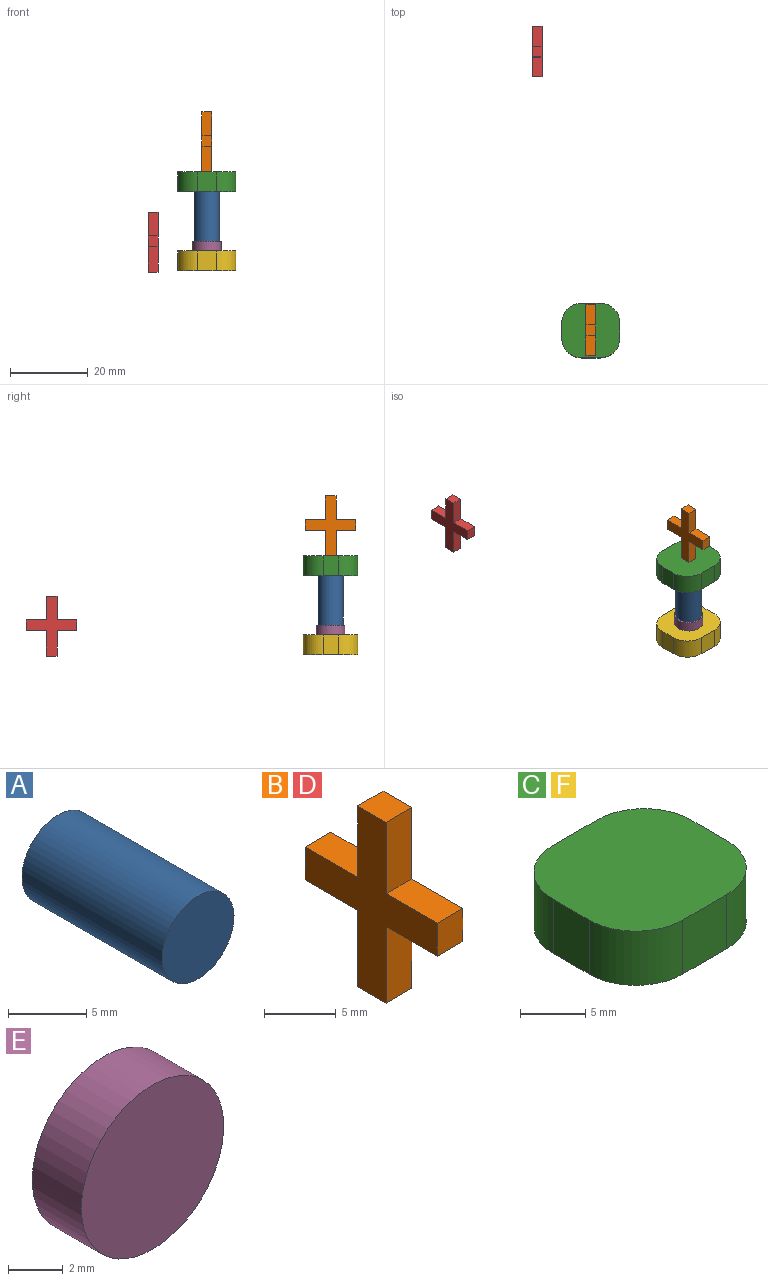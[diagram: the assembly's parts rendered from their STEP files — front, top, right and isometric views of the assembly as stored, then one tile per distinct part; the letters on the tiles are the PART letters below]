
ASSEMBLY  parts=6 mates=4
PART A: 3 faces, bbox 6.5x12.7x6.5 mm
  f0: cylinder r=3.26mm len=12.7mm, axis (0,1,0), area 259.8mm2, adj f1,f2
  f1: plane 6.51x6.51mm, normal (0,-1,0), area 33.3mm2, adj f0
  f2: plane 6.51x6.51mm, normal (0,1,0), area 33.3mm2, adj f0
PART B: 14 faces, bbox 2.5x13x15.4 mm
  f0: plane 2.8x2.54mm, normal (0,0,-1), area 7.1mm2, adj f1,f11,f12,f13
  f1: plane 6.5x2.54mm, normal (0,1,0), area 16.5mm2, adj f0,f2,f12,f13
  f2: plane 5.17x2.54mm, normal (0,0,-1), area 13.1mm2, adj f1,f3,f12,f13
  f3: plane 2.81x2.54mm, normal (0,1,0), area 7.1mm2, adj f2,f4,f12,f13
  f4: plane 5.17x2.54mm, normal (0,0,1), area 13.1mm2, adj f3,f5,f12,f13
  f5: plane 6.09x2.54mm, normal (0,1,0), area 15.5mm2, adj f4,f6,f12,f13
  f6: plane 2.8x2.54mm, normal (0,0,1), area 7.1mm2, adj f5,f7,f12,f13
  f7: plane 6.09x2.54mm, normal (0,-1,0), area 15.5mm2, adj f6,f8,f12,f13
  f8: plane 5.04x2.54mm, normal (0,0,1), area 12.8mm2, adj f7,f9,f12,f13
  f9: plane 2.81x2.54mm, normal (0,-1,0), area 7.1mm2, adj f8,f10,f12,f13
  f10: plane 5.04x2.54mm, normal (0,0,-1), area 12.8mm2, adj f9,f11,f12,f13
  f11: plane 6.5x2.54mm, normal (0,-1,0), area 16.5mm2, adj f0,f10,f12,f13
  f12: plane 15.4x13.01mm, normal (1,0,0), area 71.8mm2, adj f0,f1,f2,f3,f4,f5,f6,f7
  f13: plane 15.4x13.01mm, normal (-1,0,0), area 71.8mm2, adj f0,f1,f2,f3,f4,f5,f6,f7
PART C: 10 faces, bbox 14.9x14x5.1 mm
  f0: plane 5.08x4.76mm, normal (0,1,0), area 24.2mm2, adj f4,f5,f6,f9
  f1: plane 5.08x3.89mm, normal (-1,0,0), area 19.7mm2, adj f4,f5,f6,f7
  f2: plane 5.08x4.76mm, normal (0,-1,0), area 24.2mm2, adj f4,f5,f7,f8
  f3: plane 5.08x3.89mm, normal (1,0,0), area 19.7mm2, adj f4,f5,f8,f9
  f4: plane 14.92x14.05mm, normal (0,0,1), area 187.5mm2, adj f0,f1,f2,f3,f6,f7,f8,f9
  f5: plane 14.92x14.05mm, normal (0,0,-1), area 187.5mm2, adj f0,f1,f2,f3,f6,f7,f8,f9
  f6: cylinder r=5.08mm len=5.08mm, axis (0,0,1), area 40.5mm2, adj f0,f1,f4,f5
  f7: cylinder r=5.08mm len=5.08mm, axis (0,0,-1), area 40.5mm2, adj f1,f2,f4,f5
  f8: cylinder r=5.08mm len=5.08mm, axis (0,0,1), area 40.5mm2, adj f2,f3,f4,f5
  f9: cylinder r=5.08mm len=5.08mm, axis (0,0,-1), area 40.5mm2, adj f0,f3,f4,f5
PART D: same geometry as B
PART E: 3 faces, bbox 7.4x2.5x7.4 mm
  f0: cylinder r=3.68mm len=7.37mm, axis (0,1,0), area 58.8mm2, adj f1,f2
  f1: plane 7.37x7.37mm, normal (0,-1,0), area 42.6mm2, adj f0
  f2: plane 7.37x7.37mm, normal (0,1,0), area 42.6mm2, adj f0
PART F: same geometry as C
PLACE A rot(axis=(-1,0,0),90deg) t=(1.27,-4.77,-2.04)mm
PLACE B t=(0,-3.37,-23.59)mm
PLACE C t=(1.27,-4.77,10.66)mm
PLACE D t=(-13.81,68.31,-49.34)mm
PLACE E rot(axis=(-1,0,0),90deg) t=(1.27,-4.77,-4.58)mm
PLACE F rot(axis=(1,0,0),0deg) t=(1.27,-4.77,-9.66)mm
MATE fastened C.f4 <-> B.f0  axis (0,0,1) through (1.27,-4.77,15.74)mm
MATE fastened F.f4 <-> E.f0  axis (0,0,1) through (1.27,-4.77,-4.58)mm
MATE fastened A.f0 <-> C.f5  axis (0,0,1) through (1.27,-4.77,10.66)mm
MATE fastened E.f0 <-> A.f0  axis (0,0,1) through (1.27,-4.77,-2.04)mm
